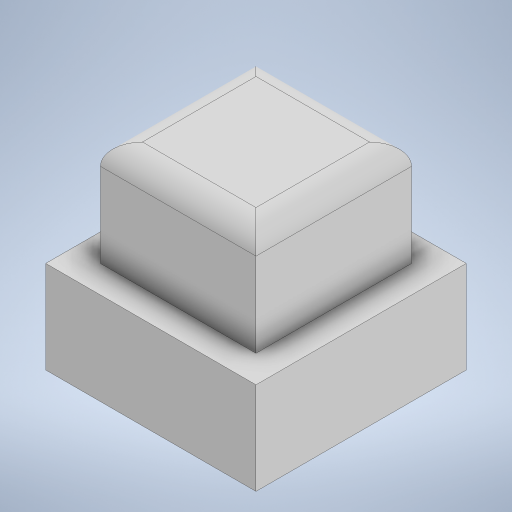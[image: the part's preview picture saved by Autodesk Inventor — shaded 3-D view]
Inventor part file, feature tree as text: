
AUTODESK INVENTOR PART (.ipt)
format: ipt  version: 2024 (Build 280153000, 153)  size: 262,144 bytes
history: native  units: mm
features: extrude x3, sketch x3, fillet x1
ambient origin geometry x8: Origin, YZ Plane, XZ Plane, XY Plane, X Axis, Y Axis, Z Axis, Center Point
bodies: Body1 (feature_tree)
feature tree (7):
  extrude  "Extrusion5"  Depth=5.0mm
  extrude  "Extrusion6"  Depth=5.0mm
  extrude  "Extrusion7"  Depth=2.195mm TaperAngle=0.0deg
  fillet  "Congé2"  Radius=3.7mm
  sketch  "Esquisse6"
  sketch  "Esquisse7"
  sketch  "Esquisse8"
